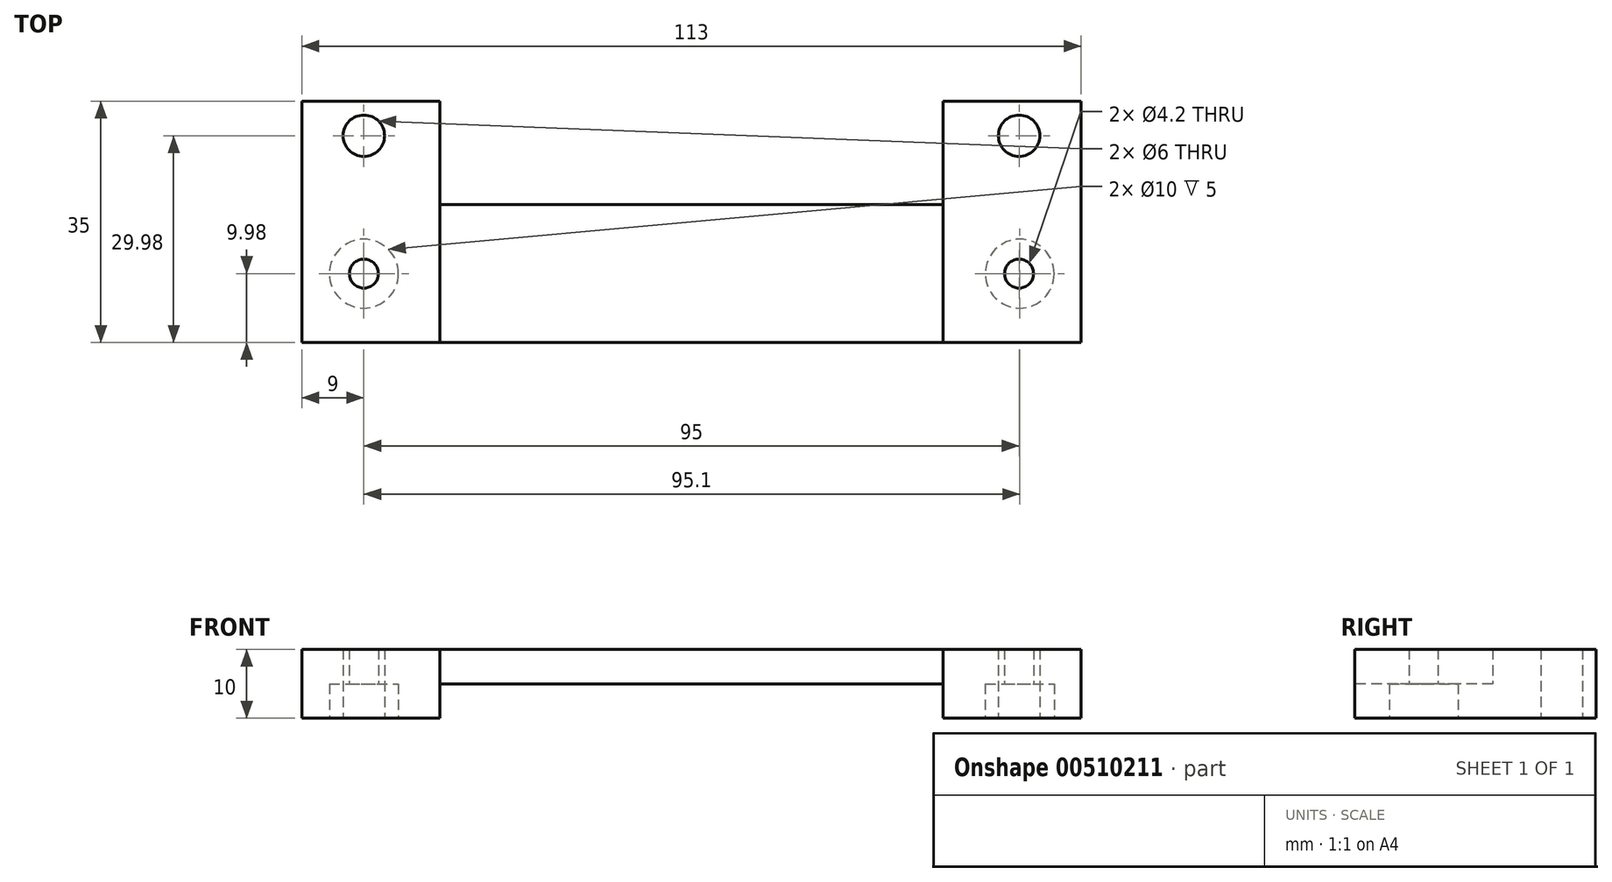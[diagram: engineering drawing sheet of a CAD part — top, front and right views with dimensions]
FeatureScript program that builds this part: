
annotation { "Feature Type Name" : "Feature", "Feature Type Description" : "" }
export const myFeature = defineFeature(function(context is Context, id is Id, definition is map)
    precondition{}
    {
        {
            var Q0;
            Q0=qCreatedBy(makeId("Top.planeOp"),FACE);
            var sketch = newSketch(context, id + "F0", { "sketchPlane" : qUnion([Q0])});
            skLineSegment(sketch, "E0", {"start": v(20, 20) * mm, "end": v(93, 20) * mm});
            skLineSegment(sketch, "E1", {"start": v(93, 0) * mm, "end": v(20, 0) * mm});
            skLineSegment(sketch, "E2", {"start": v(20, 20) * mm, "end": v(20, 0) * mm});
            skLineSegment(sketch, "E3", {"start": v(93, 20) * mm, "end": v(93, 0) * mm});
            skSolve(sketch);
        }
        {
            var Q0;
            Q0=makeQuery(id+"F0.imprint","IMPRINT",FACE,{"disambiguationData":[TD([[makeQuery(id+"F0.imprint","IMPRINT",EDGE,{"derivedFrom":sQuery(id+"F0.wireOp",EDGE,"E0")}),-1.0]])]});
            extrude(context, id + "F1", {"entities" : qUnion([Q0]), "depth" : 5 * mm});
        }
        {
            var Q0;
            Q0=makeQuery(id+"F1.opExtrude","CAP_FACE",FACE,{"disambiguationData":[OSD([sQuery(id+"F0.wireOp",EDGE,"E0"),sQuery(id+"F0.wireOp",EDGE,"E1"),sQuery(id+"F0.wireOp",EDGE,"E2"),sQuery(id+"F0.wireOp",EDGE,"E3")])],"isStart":false});
            var sketch = newSketch(context, id + "F2", { "sketchPlane" : qUnion([Q0])});
            skLineSegment(sketch, "E4.bottom", {"start": v(0, 0) * mm, "end": v(20, 0) * mm});
            skLineSegment(sketch, "E4.top", {"start": v(0, 35) * mm, "end": v(20, 35) * mm});
            skLineSegment(sketch, "E4.left", {"start": v(0, 0) * mm, "end": v(0, 35) * mm});
            skLineSegment(sketch, "E4.right", {"start": v(20, 0) * mm, "end": v(20, 35) * mm});
            skLineSegment(sketch, "E5.bottom", {"start": v(93, 0) * mm, "end": v(113, 0) * mm});
            skLineSegment(sketch, "E5.top", {"start": v(93, 35) * mm, "end": v(113, 35) * mm});
            skLineSegment(sketch, "E5.left", {"start": v(93, 0) * mm, "end": v(93, 35) * mm});
            skLineSegment(sketch, "E5.right", {"start": v(113, 0) * mm, "end": v(113, 35) * mm});
            skSolve(sketch);
        }
        {
            var Q0;
            {var subQ2=sQuery(id+"F2.wireOp",EDGE,"E4.bottom");Q0=makeQuery(id+"F2.imprint","IMPRINT",FACE,{"disambiguationData":[TD([[makeQuery(id+"F2.imprint","IMPRINT",EDGE,{"derivedFrom":subQ2}),1.0]])]});}
            var Q1;
            {var subQ3=sQuery(id+"F2.wireOp",EDGE,"E5.bottom");Q1=makeQuery(id+"F2.imprint","IMPRINT",FACE,{"disambiguationData":[TD([[makeQuery(id+"F2.imprint","IMPRINT",EDGE,{"derivedFrom":subQ3}),1.0]])]});}
            extrude(context, id + "F3", {"entities" : qUnion([Q0, Q1]), "oppositeDirection" : true, "depth" : 10 * mm});
        }
        {
            var Q0;
            Q0=makeQuery(id+"F3.opExtrude","CAP_FACE",FACE,{"disambiguationData":[OSD([sQuery(id+"F2.wireOp",EDGE,"E4.bottom"),sQuery(id+"F2.wireOp",EDGE,"E4.top"),sQuery(id+"F2.wireOp",EDGE,"E4.left"),sQuery(id+"F2.wireOp",EDGE,"E4.right")])],"isStart":false});
            var sketch = newSketch(context, id + "F4", { "sketchPlane" : qUnion([Q0])});
            skCircle(sketch, "E6", {"center": v(9, -9.98) * mm, "radius": 2.1 * mm});
            skCircle(sketch, "E7", {"center": v(9, -29.98) * mm, "radius": 3 * mm});
            skCircle(sketch, "E8", {"center": v(104, -9.98) * mm, "radius": 2.1 * mm});
            skCircle(sketch, "E9", {"center": v(104, -29.98) * mm, "radius": 3 * mm});
            skCircle(sketch, "E10", {"center": v(9, -9.98) * mm, "radius": 5 * mm});
            skCircle(sketch, "E11", {"center": v(104, -9.98) * mm, "radius": 5 * mm});
            skSolve(sketch);
        }
        {
            var Q0;
            Q0=makeQuery(id+"F4.imprint","IMPRINT",FACE,{"disambiguationData":[TD([[makeQuery(id+"F4.imprint","IMPRINT",EDGE,{"derivedFrom":sQuery(id+"F4.wireOp",EDGE,"E6")}),1.0]])]});
            var Q1;
            Q1=makeQuery(id+"F4.imprint","IMPRINT",FACE,{"disambiguationData":[TD([[makeQuery(id+"F4.imprint","IMPRINT",EDGE,{"derivedFrom":sQuery(id+"F4.wireOp",EDGE,"E7")}),1.0]])]});
            var Q2;
            Q2=makeQuery(id+"F4.imprint","IMPRINT",FACE,{"disambiguationData":[TD([[makeQuery(id+"F4.imprint","IMPRINT",EDGE,{"derivedFrom":sQuery(id+"F4.wireOp",EDGE,"E8")}),1.0]])]});
            var Q3;
            Q3=makeQuery(id+"F4.imprint","IMPRINT",FACE,{"disambiguationData":[TD([[makeQuery(id+"F4.imprint","IMPRINT",EDGE,{"derivedFrom":sQuery(id+"F4.wireOp",EDGE,"E9")}),1.0]])]});
            extrude(context, id + "F5", {"entities" : qUnion([Q0, Q1, Q2, Q3]), "operationType" : NewBodyOperationType.REMOVE, "oppositeDirection" : true, "depth" : 25 * mm});
        }
        {
            var Q0;
            Q0=makeQuery(id+"F3.opExtrude","CAP_FACE",FACE,{"disambiguationData":[OSD([sQuery(id+"F2.wireOp",EDGE,"E4.bottom"),sQuery(id+"F2.wireOp",EDGE,"E4.top"),sQuery(id+"F2.wireOp",EDGE,"E4.left"),sQuery(id+"F2.wireOp",EDGE,"E4.right")])],"isStart":false});
            var sketch = newSketch(context, id + "F6", { "sketchPlane" : qUnion([Q0])});
            skCircle(sketch, "E12", {"center": v(9, -9.98) * mm, "radius": 5 * mm});
            skCircle(sketch, "E13", {"center": v(104.1, -9.98) * mm, "radius": 5 * mm});
            skSolve(sketch);
        }
        {
            var Q0;
            Q0=makeQuery(id+"F6.imprint","IMPRINT",FACE,{"disambiguationData":[TD([[makeQuery(id+"F6.imprint","IMPRINT",EDGE,{"derivedFrom":sQuery(id+"F6.wireOp",EDGE,"E12")}),1.0]])]});
            var Q1;
            Q1=makeQuery(id+"F6.imprint","IMPRINT",FACE,{"disambiguationData":[TD([[makeQuery(id+"F6.imprint","IMPRINT",EDGE,{"derivedFrom":sQuery(id+"F6.wireOp",EDGE,"E13")}),1.0]])]});
            extrude(context, id + "F7", {"entities" : qUnion([Q0, Q1]), "operationType" : NewBodyOperationType.REMOVE, "oppositeDirection" : true, "depth" : 5 * mm});
        }
    });
